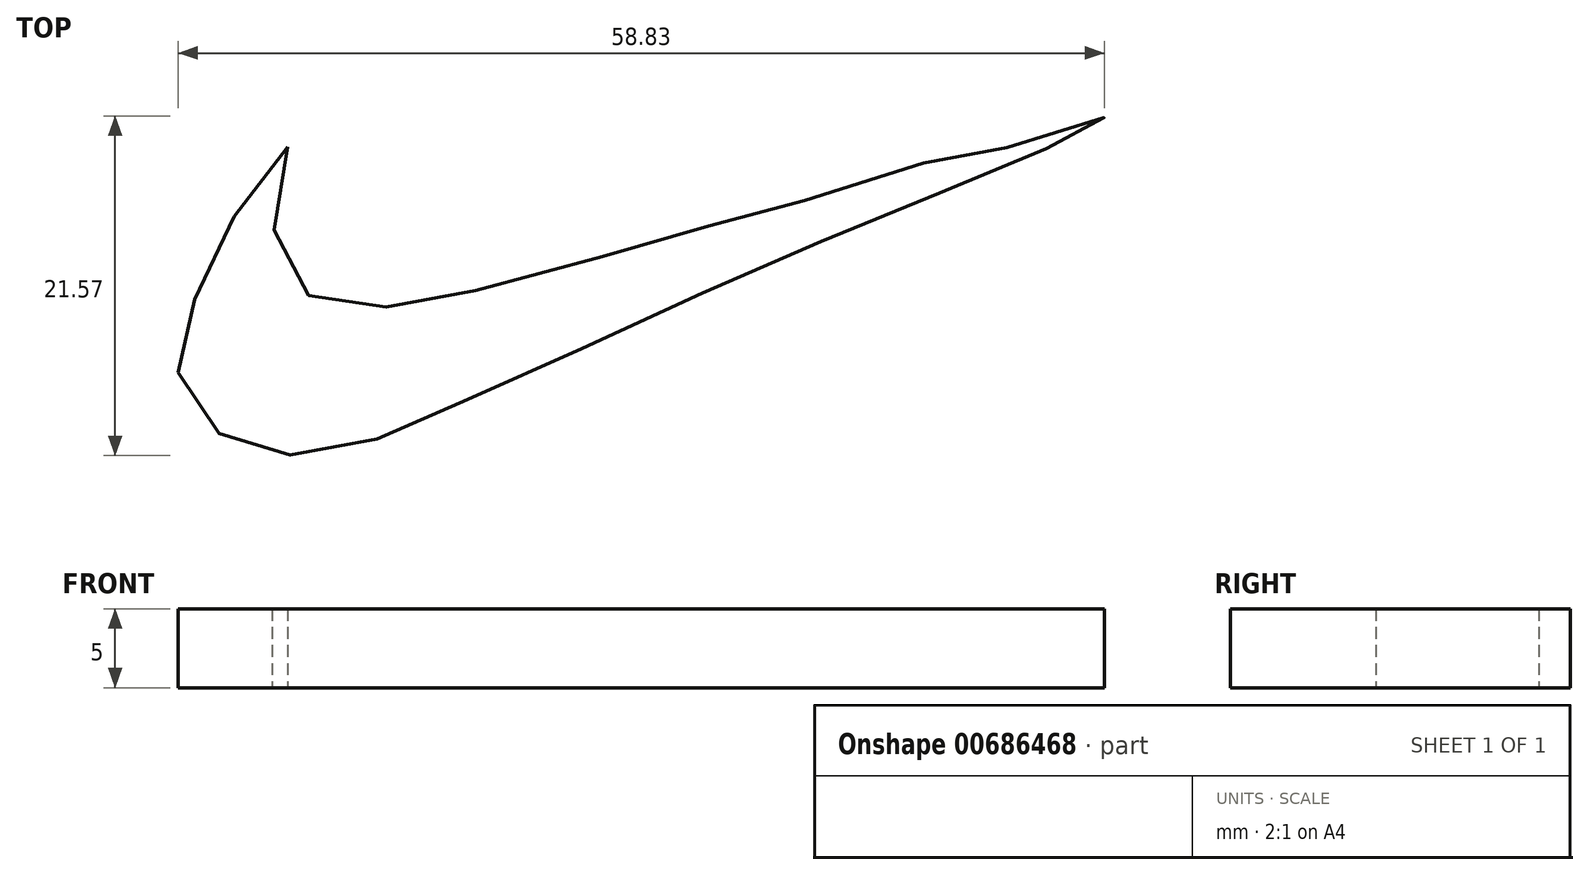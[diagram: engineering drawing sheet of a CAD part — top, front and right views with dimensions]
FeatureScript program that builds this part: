
annotation { "Feature Type Name" : "Feature", "Feature Type Description" : "" }
export const myFeature = defineFeature(function(context is Context, id is Id, definition is map)
    precondition{}
    {
        {
            var Q0;
            Q0=qCreatedBy(makeId("Top.planeOp"),FACE);
            var sketch = newSketch(context, id + "F0", { "sketchPlane" : qUnion([Q0])});
            skFitSpline(sketch, "E0", {"points": [v(-60.08, 38.69) * mm, v(-62.62, 35.56) * mm, v(-65.36, 30.68) * mm, v(-66.72, 26.38) * mm, v(-66.92, 23.84) * mm, v(-64.97, 20.9) * mm, v(-62.23, 19.54) * mm, v(-58.32, 19.15) * mm, v(-53.44, 20.52) * mm, v(-47.77, 23.06) * mm, v(-38.59, 27.16) * mm, v(-29.21, 31.46) * mm, v(-20.03, 35.17) * mm, v(-12.21, 38.5) * mm, v(-8.5, 39.86) * mm, v(-8.3, 40.64) * mm, v(-14.95, 38.5) * mm, v(-18.66, 37.9) * mm, v(-27.06, 35.36) * mm, v(-32.92, 33.8) * mm, v(-39.76, 31.85) * mm, v(-49.33, 29.3) * mm, v(-53.83, 28.53) * mm, v(-58.13, 28.72) * mm, v(-59.7, 31.07) * mm, v(-61.06, 34.58) * mm, v(-60.08, 38.69) * mm]});
            skSolve(sketch);
        }
        {
            var Q0;
            Q0 = qSketchRegion(id + "F0", true);
            extrude(context, id + "F1", {"entities" : qUnion([Q0]), "depth" : 5 * mm, "offsetDistance" : 25.4 * mm});
        }
    });
